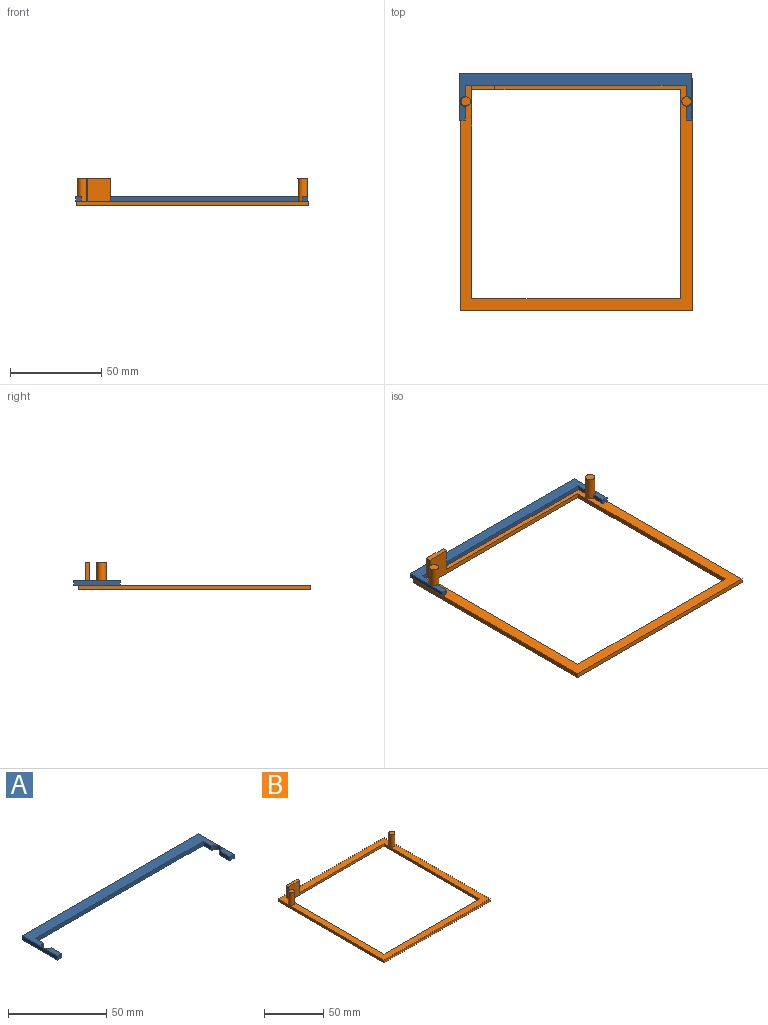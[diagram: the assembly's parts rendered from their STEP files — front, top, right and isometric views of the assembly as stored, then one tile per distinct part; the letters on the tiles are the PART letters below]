
ASSEMBLY  parts=2 mates=1
PART A: 14 faces, bbox 127x25.4x2.5 mm
  f0: plane 6.11x2.54mm, normal (1,0,0), area 15.5mm2, adj f3,f4,f11,f13
  f1: plane 6.11x2.54mm, normal (-1,0,0), area 15.5mm2, adj f3,f4,f11,f12
  f2: plane 3.18x2.54mm, normal (0,-1,0), area 8.1mm2, adj f3,f4,f7,f9
  f3: plane 127x25.4mm, normal (0,0,1), area 900.1mm2, adj f0,f1,f2,f5,f6,f7,f8,f9
  f4: plane 127x25.4mm, normal (0,0,-1), area 900.1mm2, adj f0,f1,f2,f5,f6,f7,f8,f9
  f5: plane 25.4x2.54mm, normal (1,0,0), area 64.5mm2, adj f3,f4,f6,f8
  f6: plane 127x2.54mm, normal (0,1,0), area 322.6mm2, adj f3,f4,f5,f7
  f7: plane 25.4x2.54mm, normal (-1,0,0), area 64.5mm2, adj f2,f3,f4,f6
  f8: plane 3.18x2.54mm, normal (0,-1,0), area 8.1mm2, adj f3,f4,f5,f10
  f9: plane 7.38x2.54mm, normal (1,0,0), area 18.7mm2, adj f2,f3,f4,f13
  f10: plane 7.38x2.54mm, normal (-1,0,0), area 18.7mm2, adj f3,f4,f8,f12
  f11: plane 120.65x2.54mm, normal (0,-1,0), area 306.5mm2, adj f0,f1,f3,f4
  f12: cylinder r=2.79mm len=5.59mm, axis (0,0,1), area 23.6mm2, adj f1,f3,f4,f10
  f13: cylinder r=2.79mm len=5.59mm, axis (0,0,1), area 23.6mm2, adj f0,f3,f4,f9
PART B: 18 faces, bbox 127x127x15.2 mm
  f0: plane 127x127mm, normal (0,0,1), area 2991.7mm2, adj f1,f2,f3,f4,f5,f6,f7,f8
  f1: plane 114.3x15.24mm, normal (0,-1,0), area 451.6mm2, adj f0,f2,f8,f9,f14,f15,f17
  f2: plane 114.3x2.54mm, normal (-1,0,0), area 290.3mm2, adj f0,f1,f3,f9
  f3: plane 114.3x2.54mm, normal (0,1,0), area 290.3mm2, adj f0,f2,f8,f9
  f4: plane 127x2.54mm, normal (1,0,0), area 322.6mm2, adj f0,f5,f7,f9
  f5: plane 127x2.54mm, normal (0,1,0), area 322.6mm2, adj f0,f4,f6,f9
  f6: plane 127x2.54mm, normal (-1,0,0), area 322.6mm2, adj f0,f5,f7,f9
  f7: plane 127x2.54mm, normal (0,-1,0), area 322.6mm2, adj f0,f4,f6,f9
  f8: plane 114.3x2.54mm, normal (1,0,0), area 290.3mm2, adj f0,f1,f3,f9
  f9: plane 127x127mm, normal (0,0,-1), area 3064.5mm2, adj f1,f2,f3,f4,f5,f6,f7,f8
  f10: cylinder r=2.54mm len=12.7mm, axis (0,0,-1), area 202.7mm2, adj f0,f11
  f11: plane 5.08x5.08mm, normal (0,0,1), area 20.3mm2, adj f10
  f12: cylinder r=2.54mm len=12.7mm, axis (0,0,-1), area 202.7mm2, adj f0,f13
  f13: plane 5.08x5.08mm, normal (0,0,1), area 20.3mm2, adj f12
  f14: plane 12.7x2.54mm, normal (-1,0,0), area 32.3mm2, adj f0,f1,f16,f17
  f15: plane 12.7x2.54mm, normal (1,0,0), area 32.3mm2, adj f0,f1,f16,f17
  f16: plane 12.7x12.7mm, normal (0,1,0), area 161.3mm2, adj f0,f14,f15,f17
  f17: plane 12.7x2.54mm, normal (0,0,1), area 32.3mm2, adj f1,f14,f15,f16
PLACE A t=(-0.25,53.34,2.54)mm
PLACE B at identity fixed
MATE cylindrical B.f12 <-> A.f12  axis (0,0,-1) through (60.32,50.8,2.54)mm
